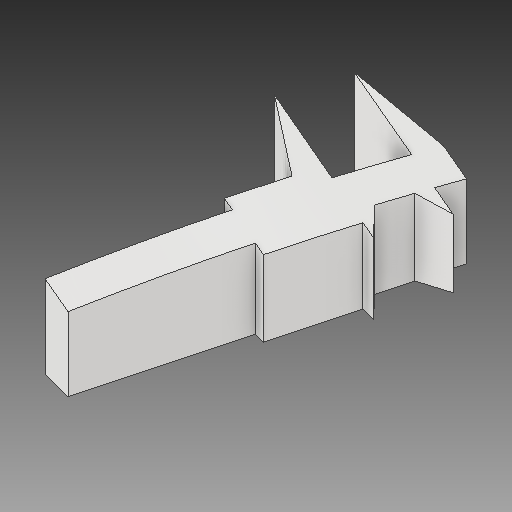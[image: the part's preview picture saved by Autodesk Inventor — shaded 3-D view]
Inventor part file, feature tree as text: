
AUTODESK INVENTOR PART (.ipt)
format: ipt  version: 2017 (Build 210142000, 142)  size: 536,064 bytes
history: native  units: in
note: dims shown in document units (in); Inventor stores cm internally (conversion verified against a paired STEP export)
features: reference x5, sketch x3, extrude x2, revolve x1, projected_geometry x1
ambient origin geometry x8: Origin, YZ Plane, XZ Plane, XY Plane, X Axis, Y Axis, Z Axis, Center Point
bodies: Solid1 (feature_tree)
feature tree (12):
  revolve  "Revolution1"  [1 undecoded]
  extrude  "Extrusion1"  Depth=0.1in
  extrude  "Extrusion2"  Depth=0.275in
  sketch  "Sketch1"  dims[d0=0.8265in d1=0.175in]
  sketch  "Sketch2"  dims[d2=0.05in d3=0.1in]
  projected_geometry  "Projected Loop1"
  reference  "Reference1"
  reference  "Reference2"
  reference  "Reference3"
  sketch  "Sketch3"  dims[d4=0.15in d5=0.275in d6=90.0deg d7=1.55in d9=1.0in d11=0.025in d13=1.0in d14=0.025in d15=0.0125in d16=0.6536in d17=0.0125in d18=0.1in d19=0.05in d20=0.05in d21=0.025in d22=0.0125in d23=0.29in d24=0.0125in d25=0.1in d26=0.3in d27=0.1in d28=0.025in d29=0.015in d30=0.015in d31=0.025in d32=0.0125in d33=0.225in d34=0.1in d35=1.1in d36=0.025in d38=60.0deg d39=0.075in d40=0.0in d41=0.0in d42=0.125in d43=0.125in d44=0.04in d45=0.05in d46=0.04in d47=0.04in d49=0.025in d50=0.125in d51=0.5in d52=0.085in d53=0.1in d54=1.0in d55=0.025in d56=1.0054in d57=1.0054in d58=15.0deg d59=0.04in d60=0.025in d61=0.5in d62=0.0in]
  reference  "Reference4"
  reference  "Reference5"
note: 1 required parameter value undecoded (feature->parameter linkage not recoverable at this tier; creation-order binding heuristic only, values carry confidence <= 0.55)
